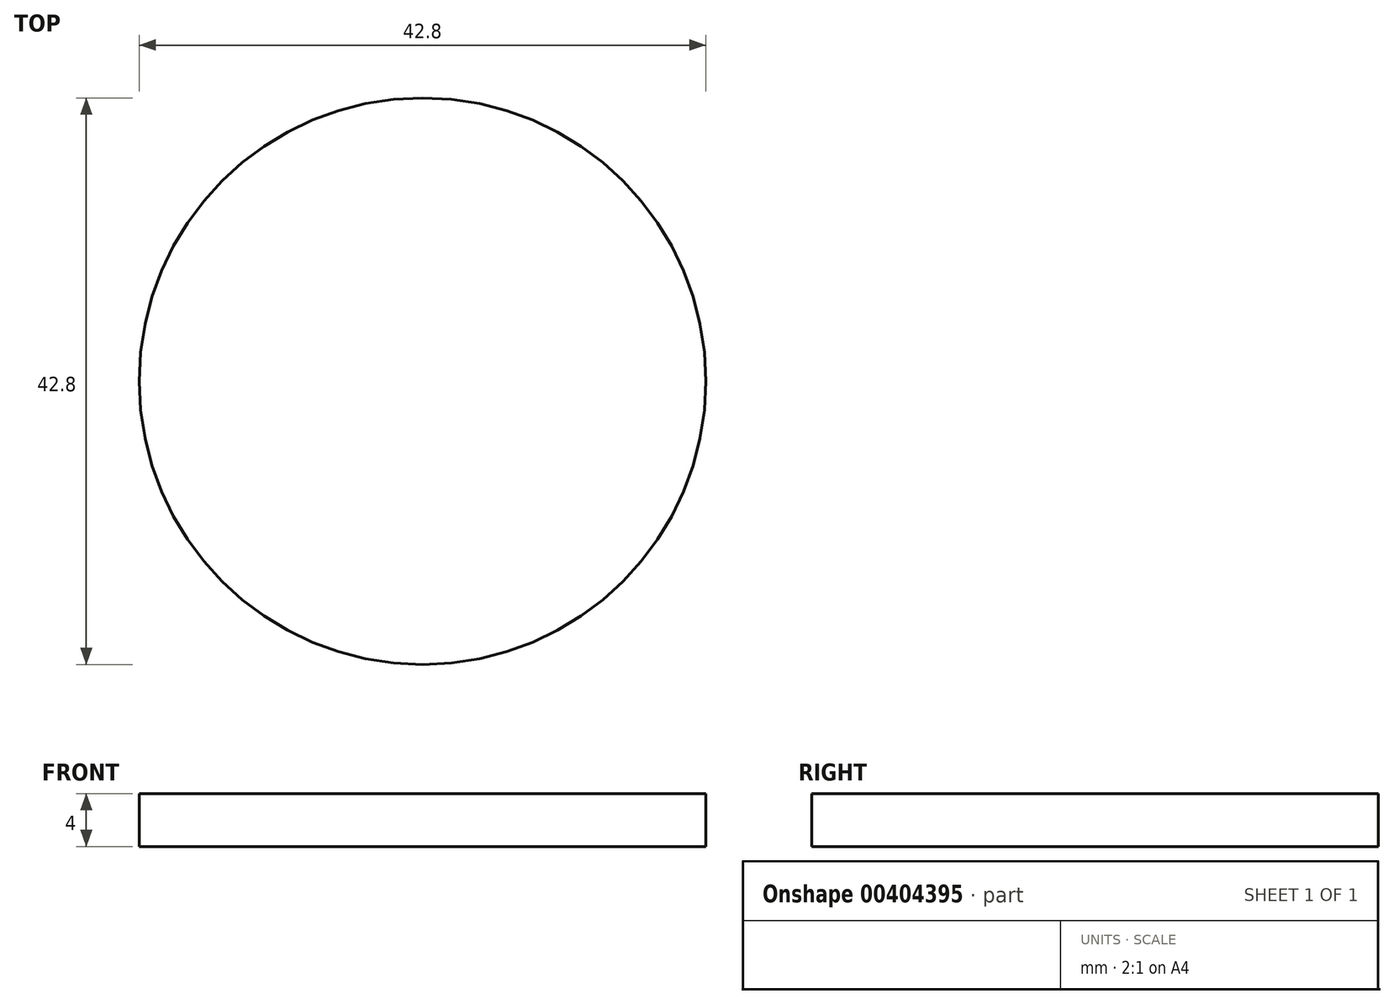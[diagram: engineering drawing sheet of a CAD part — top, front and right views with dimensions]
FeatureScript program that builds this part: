
annotation { "Feature Type Name" : "Feature", "Feature Type Description" : "" }
export const myFeature = defineFeature(function(context is Context, id is Id, definition is map)
    precondition{}
    {
        {
            var Q0;
            Q0=qCreatedBy(makeId("Top.planeOp"),FACE);
            var sketch = newSketch(context, id + "F0", { "sketchPlane" : qUnion([Q0])});
            skCircle(sketch, "E0", {"center": v(0, 0) * mm, "radius": 21.4 * mm});
            skSolve(sketch);
        }
        {
            var Q0;
            Q0=makeQuery(id+"F0.imprint","IMPRINT",FACE,{"disambiguationData":[TD([[makeQuery(id+"F0.imprint","IMPRINT",EDGE,{"derivedFrom":sQuery(id+"F0.wireOp",EDGE,"E0")}),1.0]])]});
            extrude(context, id + "F1", {"entities" : qUnion([Q0]), "depth" : 4 * mm});
        }
    });
